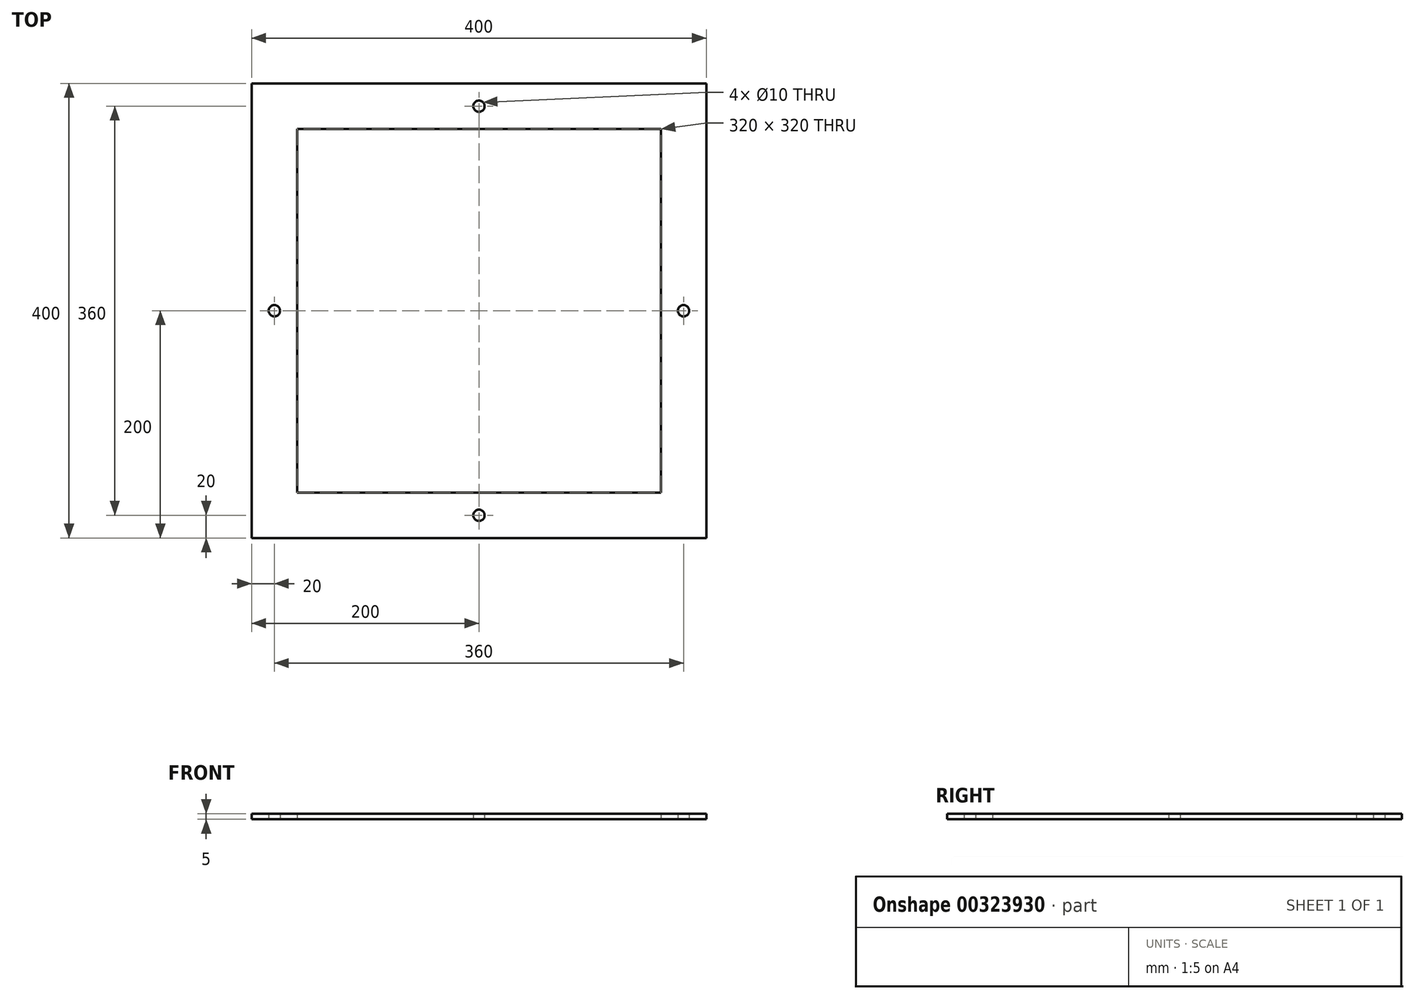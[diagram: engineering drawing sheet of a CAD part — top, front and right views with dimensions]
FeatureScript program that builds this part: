
annotation { "Feature Type Name" : "Feature", "Feature Type Description" : "" }
export const myFeature = defineFeature(function(context is Context, id is Id, definition is map)
    precondition{}
    {
        {
            var Q0;
            Q0=qCreatedBy(makeId("Top.planeOp"),FACE);
            var sketch = newSketch(context, id + "F0", { "sketchPlane" : qUnion([Q0])});
            skLineSegment(sketch, "E0.bottom", {"start": v(-200, 200) * mm, "end": v(200, 200) * mm});
            skLineSegment(sketch, "E0.top", {"start": v(-200, -200) * mm, "end": v(200, -200) * mm});
            skLineSegment(sketch, "E0.right", {"start": v(200, 200) * mm, "end": v(200, -200) * mm});
            skLineSegment(sketch, "E1", {"start": v(-200, 200) * mm, "end": v(-200, -200) * mm});
            skCircle(sketch, "E2", {"center": v(-180, 0) * mm, "radius": 5 * mm});
            skCircle(sketch, "E3", {"center": v(0, 180) * mm, "radius": 5 * mm});
            skCircle(sketch, "E4", {"center": v(0, -180) * mm, "radius": 5 * mm});
            skCircle(sketch, "E5", {"center": v(180, 0) * mm, "radius": 5 * mm});
            skLineSegment(sketch, "E6.bottom", {"start": v(160, 160) * mm, "end": v(-160, 160) * mm});
            skLineSegment(sketch, "E6.top", {"start": v(160, -160) * mm, "end": v(-160, -160) * mm});
            skLineSegment(sketch, "E6.left", {"start": v(160, 160) * mm, "end": v(160, -160) * mm});
            skLineSegment(sketch, "E6.right", {"start": v(-160, 160) * mm, "end": v(-160, -160) * mm});
            skSolve(sketch);
        }
        {
            var Q0;
            {var subQ3=sQuery(id+"F0.wireOp",EDGE,"E0.bottom");Q0=makeQuery(id+"F0.imprint","IMPRINT",FACE,{"disambiguationData":[TD([[makeQuery(id+"F0.imprint","IMPRINT",EDGE,{"derivedFrom":subQ3}),-1.0]])]});}
            extrude(context, id + "F1", {"entities" : qUnion([Q0]), "depth" : 5 * mm});
        }
    });
